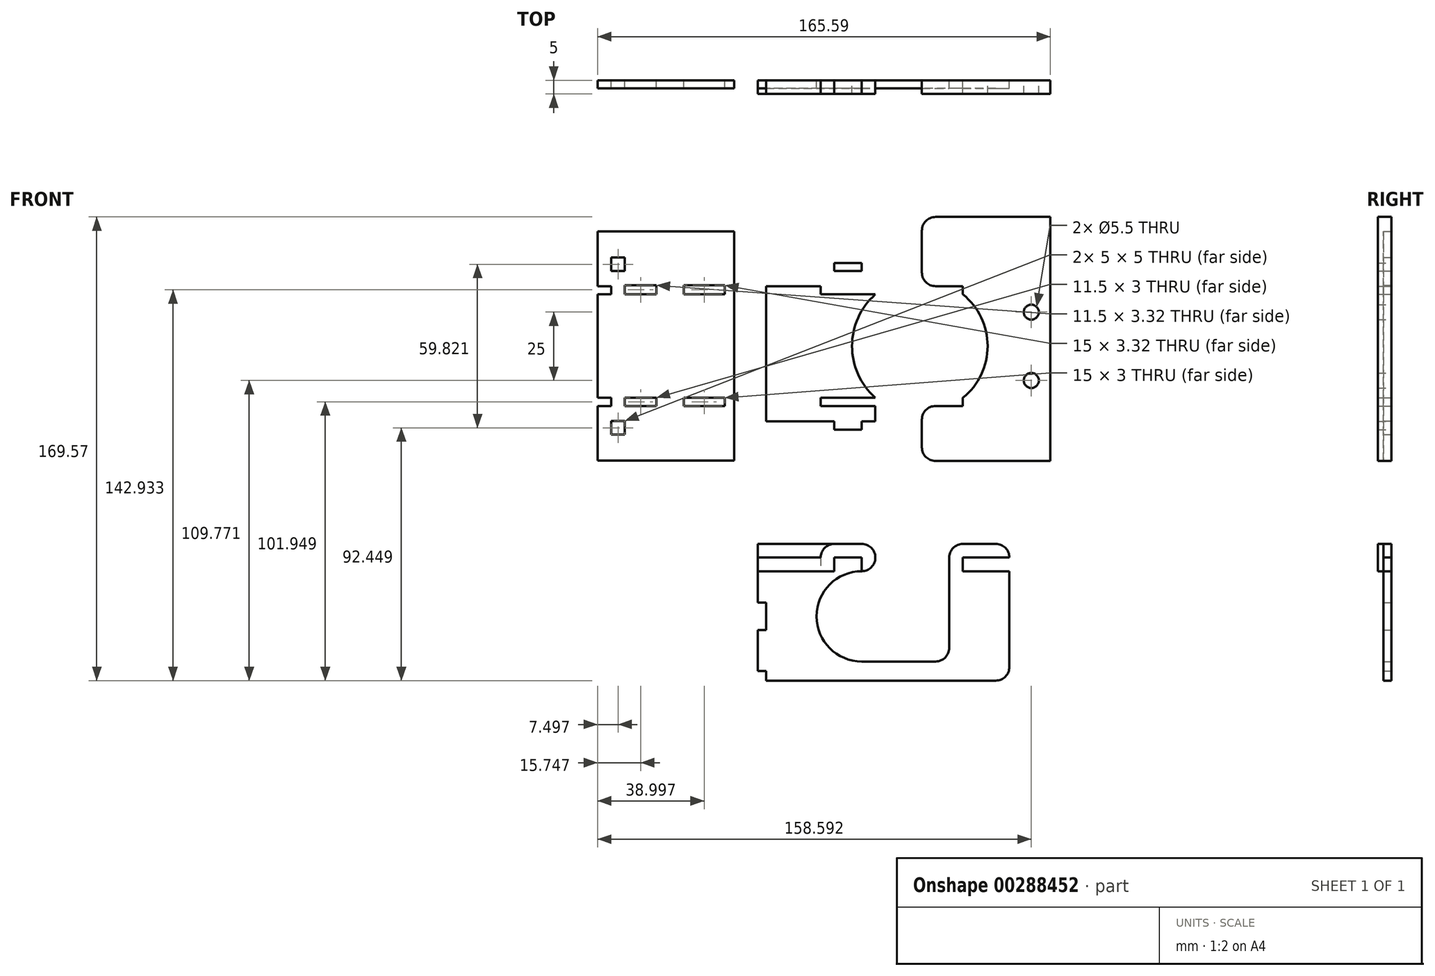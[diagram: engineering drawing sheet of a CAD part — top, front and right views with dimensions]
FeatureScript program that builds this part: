
annotation { "Feature Type Name" : "Feature", "Feature Type Description" : "" }
export const myFeature = defineFeature(function(context is Context, id is Id, definition is map)
    precondition{}
    {
        {
            var Q0;
            Q0=qCreatedBy(makeId("Front.planeOp"),FACE);
            var sketch = newSketch(context, id + "F0", { "sketchPlane" : qUnion([Q0])});
            skLineSegment(sketch, "E0.right", {"start": v(-7.94, 96.43) * mm, "end": v(-7.94, 31.43) * mm});
            skCircle(sketch, "E1", {"center": v(-14.94, 76.43) * mm, "radius": 2.75 * mm});
            skCircle(sketch, "E2", {"center": v(-14.94, 51.43) * mm, "radius": 2.75 * mm});
            skLineSegment(sketch, "E3", {"start": v(-7.94, 63.93) * mm, "end": v(-14.94, 63.93) * mm, "construction": true});
            skLineSegment(sketch, "E4", {"start": v(-14.94, 63.93) * mm, "end": v(-111.94, 63.93) * mm, "construction": true});
            skPoint(sketch, "E5.middle", {"position": v(-52.94, 63.93) * mm});
            skLineSegment(sketch, "E6", {"start": v(-71.94, 82.93) * mm, "end": v(-71.94, 91.43) * mm, "construction": true});
            skLineSegment(sketch, "E7", {"start": v(-71.94, 91.43) * mm, "end": v(-71.94, 82.93) * mm, "construction": true});
            skLineSegment(sketch, "E8", {"start": v(-71.94, 42.1) * mm, "end": v(-71.94, 36.43) * mm, "construction": true});
            skLineSegment(sketch, "E9", {"start": v(-71.94, 85.93) * mm, "end": v(-111.94, 85.93) * mm});
            skLineSegment(sketch, "E10", {"start": v(-111.94, 85.93) * mm, "end": v(-111.94, 91.43) * mm});
            skLineSegment(sketch, "E11", {"start": v(-111.94, 91.43) * mm, "end": v(-71.94, 91.43) * mm});
            skLineSegment(sketch, "E12", {"start": v(-71.94, 42.1) * mm, "end": v(-111.94, 42.1) * mm});
            skLineSegment(sketch, "E13", {"start": v(-111.94, 42.1) * mm, "end": v(-111.94, 36.43) * mm});
            skLineSegment(sketch, "E14", {"start": v(-111.94, 36.43) * mm, "end": v(-71.94, 36.43) * mm});
            skLineSegment(sketch, "E15", {"start": v(-111.94, 91.43) * mm, "end": v(-111.94, 94.43) * mm});
            skLineSegment(sketch, "E16", {"start": v(-111.94, 33.43) * mm, "end": v(-111.94, 42.1) * mm});
            skLineSegment(sketch, "E17", {"start": v(-111.94, 42.1) * mm, "end": v(-111.94, 45.1) * mm});
            skLineSegment(sketch, "E18", {"start": v(-111.94, 85.93) * mm, "end": v(-111.94, 80.93) * mm});
            skLineSegment(sketch, "E19", {"start": v(-71.94, 82.93) * mm, "end": v(-71.94, 85.93) * mm});
            skLineSegment(sketch, "E20", {"start": v(-111.94, 91.43) * mm, "end": v(-91.94, 91.43) * mm});
            skLineSegment(sketch, "E21", {"start": v(-7.94, 63.93) * mm, "end": v(-22.94, 63.93) * mm, "construction": true});
            skLineSegment(sketch, "E22", {"start": v(-22.94, 63.93) * mm, "end": v(-22.94, 96.43) * mm, "construction": true});
            skLineSegment(sketch, "E23", {"start": v(-22.94, 85.93) * mm, "end": v(-22.94, 91.43) * mm});
            skLineSegment(sketch, "E24", {"start": v(-22.94, 42.1) * mm, "end": v(-22.94, 36.43) * mm});
            skLineSegment(sketch, "E25.trimOffspring", {"start": v(-22.94, 63.93) * mm, "end": v(-22.94, 31.43) * mm, "construction": true});
            skPoint(sketch, "E26.end.orphan", {"position": v(-54.94, 91.43) * mm});
            skPoint(sketch, "E27.end.orphan", {"position": v(-54.94, 36.43) * mm});
            skLineSegment(sketch, "E28", {"start": v(-54.94, 91.43) * mm, "end": v(-54.94, 85.93) * mm});
            skLineSegment(sketch, "E29", {"start": v(-54.94, 91.43) * mm, "end": v(-22.94, 91.43) * mm});
            skLineSegment(sketch, "E30", {"start": v(-22.94, 85.93) * mm, "end": v(-54.94, 85.93) * mm});
            skLineSegment(sketch, "E31", {"start": v(-54.94, 42.1) * mm, "end": v(-22.94, 42.1) * mm});
            skLineSegment(sketch, "E32", {"start": v(-22.94, 36.43) * mm, "end": v(-54.94, 36.43) * mm});
            skLineSegment(sketch, "E33.trimOffspring", {"start": v(-54.94, 42.1) * mm, "end": v(-54.94, 36.43) * mm});
            skLineSegment(sketch, "E34", {"start": v(-22.94, 80.93) * mm, "end": v(-22.94, 85.93) * mm});
            skLineSegment(sketch, "E35", {"start": v(-71.94, 85.93) * mm, "end": v(-54.94, 85.93) * mm});
            skLineSegment(sketch, "E36", {"start": v(-71.94, 42.1) * mm, "end": v(-54.94, 42.1) * mm});
            skLineSegment(sketch, "E37.trimOffspring", {"start": v(-71.94, 82.93) * mm, "end": v(-71.94, 85.93) * mm, "construction": true});
            skLineSegment(sketch, "E38", {"start": v(-22.94, 91.43) * mm, "end": v(-22.94, 96.43) * mm});
            skLineSegment(sketch, "E39", {"start": v(-22.94, 36.43) * mm, "end": v(-22.94, 31.43) * mm});
            skLineSegment(sketch, "E40", {"start": v(-71.94, 36.43) * mm, "end": v(-71.94, 33.43) * mm});
            skLineSegment(sketch, "E41", {"start": v(-76.94, 33.43) * mm, "end": v(-111.94, 33.43) * mm});
            skLineSegment(sketch, "E42", {"start": v(-71.94, 91.43) * mm, "end": v(-71.94, 94.43) * mm});
            skLineSegment(sketch, "E43", {"start": v(-76.94, 94.43) * mm, "end": v(-111.94, 94.43) * mm});
            skLineSegment(sketch, "E44", {"start": v(-111.94, 85.93) * mm, "end": v(-111.94, 82.93) * mm});
            skLineSegment(sketch, "E45", {"start": v(-111.94, 82.93) * mm, "end": v(-22.94, 82.93) * mm});
            skLineSegment(sketch, "E46", {"start": v(-22.94, 42.1) * mm, "end": v(-22.94, 45.1) * mm});
            skLineSegment(sketch, "E47", {"start": v(-22.94, 45.1) * mm, "end": v(-111.94, 45.1) * mm});
            skPoint(sketch, "E48.orphan", {"position": v(-22.94, 47.1) * mm});
            skLineSegment(sketch, "E49", {"start": v(-71.94, 91.43) * mm, "end": v(-71.94, 85.93) * mm});
            skLineSegment(sketch, "E50", {"start": v(-71.94, 42.1) * mm, "end": v(-71.94, 36.43) * mm});
            skLineSegment(sketch, "E51.trimOffspring", {"start": v(-111.94, 94.43) * mm, "end": v(-111.94, 80.93) * mm, "construction": true});
            skLineSegment(sketch, "E52.bottom", {"start": v(-111.94, 104.22) * mm, "end": v(-114.94, 104.22) * mm});
            skLineSegment(sketch, "E52.top", {"start": v(-111.94, 18.4) * mm, "end": v(-114.94, 18.4) * mm});
            skLineSegment(sketch, "E52.left", {"start": v(-111.94, 104.22) * mm, "end": v(-111.94, 18.4) * mm});
            skLineSegment(sketch, "E53", {"start": v(-71.94, 42.1) * mm, "end": v(-71.94, 45.1) * mm});
            skLineSegment(sketch, "E54.top", {"start": v(-22.94, 21.99) * mm, "end": v(-54.94, 21.99) * mm});
            skLineSegment(sketch, "E54.left", {"start": v(-22.94, 36.43) * mm, "end": v(-22.94, 29.2) * mm});
            skLineSegment(sketch, "E54.right", {"start": v(-54.94, 36.43) * mm, "end": v(-54.94, 21.99) * mm});
            skLineSegment(sketch, "E55.bottom", {"start": v(-22.94, 91.43) * mm, "end": v(-54.94, 91.43) * mm});
            skLineSegment(sketch, "E55.top", {"start": v(-22.94, 111.23) * mm, "end": v(-54.94, 111.23) * mm});
            skLineSegment(sketch, "E55.right", {"start": v(-54.94, 91.43) * mm, "end": v(-54.94, 111.23) * mm});
            skLineSegment(sketch, "E56", {"start": v(-14.94, 76.43) * mm, "end": v(-44.94, 76.43) * mm, "construction": true});
            skLineSegment(sketch, "E57", {"start": v(-44.94, 85.93) * mm, "end": v(-44.94, 111.23) * mm, "construction": true});
            skLineSegment(sketch, "E58", {"start": v(-44.94, 45.1) * mm, "end": v(-44.94, 42.1) * mm});
            skLineSegment(sketch, "E59", {"start": v(-44.94, 42.1) * mm, "end": v(-44.94, 45.1) * mm});
            skLineSegment(sketch, "E60", {"start": v(-44.94, 82.93) * mm, "end": v(-44.94, 85.93) * mm});
            skPoint(sketch, "E61.trimOffspring.end.orphan", {"position": v(-54.94, 82.93) * mm});
            skPoint(sketch, "E62.start.orphan", {"position": v(-54.94, 45.1) * mm});
            skLineSegment(sketch, "E63.trimOffspring", {"start": v(-44.94, 42.1) * mm, "end": v(-44.94, 21.99) * mm, "construction": true});
            skLineSegment(sketch, "E64", {"start": v(-111.94, 42.1) * mm, "end": v(-111.94, 36.43) * mm, "construction": true});
            skLineSegment(sketch, "E65", {"start": v(-86.94, -8.34) * mm, "end": v(-76.94, -8.34) * mm, "construction": true});
            skPoint(sketch, "E65.endSnap0", {"position": v(-22.94, 29.2) * mm});
            skLineSegment(sketch, "E66", {"start": v(-86.94, -8.34) * mm, "end": v(-76.94, -8.34) * mm});
            skLineSegment(sketch, "E67", {"start": v(-22.94, -53.34) * mm, "end": v(-22.94, -18.34) * mm});
            skLineSegment(sketch, "E68", {"start": v(-44.94, -13.34) * mm, "end": v(-44.94, -46.34) * mm, "construction": true});
            skLineSegment(sketch, "E69", {"start": v(-71.94, 45.1) * mm, "end": v(-71.94, 36.43) * mm, "construction": true});
            skLineSegment(sketch, "E70", {"start": v(-91.94, -18.34) * mm, "end": v(-91.94, -58.34) * mm, "construction": true});
            skLineSegment(sketch, "E71.trimOffspring", {"start": v(-39.94, -8.34) * mm, "end": v(-27.94, -8.34) * mm, "construction": true});
            skLineSegment(sketch, "E72.trimOffspring", {"start": v(-39.94, -8.34) * mm, "end": v(-27.94, -8.34) * mm});
            skLineSegment(sketch, "E73", {"start": v(-22.94, -18.34) * mm, "end": v(-22.94, -53.34) * mm});
            skLineSegment(sketch, "E74", {"start": v(-27.94, -58.34) * mm, "end": v(-111.94, -58.34) * mm});
            skLineSegment(sketch, "E75", {"start": v(-66.94, -51.34) * mm, "end": v(-49.94, -51.34) * mm});
            skLineSegment(sketch, "E76", {"start": v(-44.94, -46.34) * mm, "end": v(-44.94, -13.34) * mm});
            skArc(sketch, "E77.filletArc", {"start": v(-49.94, -51.34) * mm, "mid": v(-46.4, -49.87) * mm, "end": v(-44.94, -46.34) * mm});
            skPoint(sketch, "E78.visualSharp", {"position": v(-71.94, -8.34) * mm});
            skArc(sketch, "E78.filletArc", {"start": v(-71.94, -13.34) * mm, "mid": v(-73.4, -9.8) * mm, "end": v(-76.94, -8.34) * mm});
            skArc(sketch, "E79.filletArc", {"start": v(-39.94, -8.34) * mm, "mid": v(-43.47, -9.8) * mm, "end": v(-44.94, -13.34) * mm});
            skPoint(sketch, "E80.visualSharp", {"position": v(-22.94, -8.34) * mm});
            skArc(sketch, "E80.filletArc", {"start": v(-22.94, -13.34) * mm, "mid": v(-24.4, -9.8) * mm, "end": v(-27.94, -8.34) * mm});
            skArc(sketch, "E81.filletArc", {"start": v(-27.94, -58.34) * mm, "mid": v(-24.4, -56.87) * mm, "end": v(-22.94, -53.34) * mm});
            skLineSegment(sketch, "E82", {"start": v(-111.94, -34.84) * mm, "end": v(-111.94, -29.84) * mm});
            skLineSegment(sketch, "E83", {"start": v(-111.94, -29.84) * mm, "end": v(-111.94, -39.84) * mm});
            skLineSegment(sketch, "E84", {"start": v(-111.94, -39.84) * mm, "end": v(-114.94, -39.84) * mm});
            skLineSegment(sketch, "E85", {"start": v(-114.94, -29.84) * mm, "end": v(-111.94, -29.84) * mm});
            skLineSegment(sketch, "E86", {"start": v(-114.94, 104.22) * mm, "end": v(-114.94, 18.4) * mm});
            skLineSegment(sketch, "E87", {"start": v(-163.53, 82.93) * mm, "end": v(-152.03, 82.93) * mm, "construction": true});
            skLineSegment(sketch, "E88", {"start": v(-111.94, 42.1) * mm, "end": v(-114.94, 42.1) * mm, "construction": true});
            skLineSegment(sketch, "E89", {"start": v(-163.53, 45.1) * mm, "end": v(-152.03, 45.1) * mm, "construction": true});
            skLineSegment(sketch, "E90.trimOffspring", {"start": v(-111.94, -39.84) * mm, "end": v(-111.94, -29.84) * mm});
            skLineSegment(sketch, "E91", {"start": v(-163.53, 86.26) * mm, "end": v(-152.03, 86.26) * mm});
            skLineSegment(sketch, "E92", {"start": v(-127.03, 86.26) * mm, "end": v(-127.03, 82.93) * mm});
            skLineSegment(sketch, "E93", {"start": v(-142.03, 82.93) * mm, "end": v(-142.03, 86.26) * mm});
            skLineSegment(sketch, "E94", {"start": v(-152.03, 86.26) * mm, "end": v(-152.03, 82.93) * mm});
            skLineSegment(sketch, "E95", {"start": v(-142.03, 42.1) * mm, "end": v(-142.03, 45.1) * mm});
            skLineSegment(sketch, "E96.trimOffspring", {"start": v(-152.03, 45.1) * mm, "end": v(-152.03, 42.1) * mm});
            skLineSegment(sketch, "E97.trimOffspring", {"start": v(-127.03, 42.1) * mm, "end": v(-142.03, 42.1) * mm, "construction": true});
            skLineSegment(sketch, "E98.trimOffspring", {"start": v(-152.03, 42.1) * mm, "end": v(-163.53, 42.1) * mm, "construction": true});
            skLineSegment(sketch, "E99.trimOffspring", {"start": v(-142.03, 45.1) * mm, "end": v(-130.53, 45.1) * mm, "construction": true});
            skLineSegment(sketch, "E100.trimOffspring", {"start": v(-152.03, 86.26) * mm, "end": v(-163.53, 86.26) * mm, "construction": true});
            skLineSegment(sketch, "E101.trimOffspring", {"start": v(-142.03, 82.93) * mm, "end": v(-130.53, 82.93) * mm, "construction": true});
            skLineSegment(sketch, "E102.trimOffspring", {"start": v(-142.03, 86.26) * mm, "end": v(-127.03, 86.26) * mm});
            skLineSegment(sketch, "E103.trimOffspring", {"start": v(-114.94, 82.93) * mm, "end": v(-111.94, 82.93) * mm, "construction": true});
            skLineSegment(sketch, "E104.top", {"start": v(-163.53, 82.93) * mm, "end": v(-152.03, 82.93) * mm});
            skLineSegment(sketch, "E105.top", {"start": v(-142.03, 82.93) * mm, "end": v(-130.53, 82.93) * mm});
            skLineSegment(sketch, "E105.left", {"start": v(-142.03, 86.26) * mm, "end": v(-142.03, 82.93) * mm});
            skLineSegment(sketch, "E106.bottom", {"start": v(-164.07, 45.1) * mm, "end": v(-152.03, 45.1) * mm});
            skLineSegment(sketch, "E106.top", {"start": v(-163.53, 42.1) * mm, "end": v(-152.03, 42.1) * mm});
            skLineSegment(sketch, "E107.bottom", {"start": v(-142.03, 45.1) * mm, "end": v(-127.03, 45.1) * mm});
            skLineSegment(sketch, "E107.top", {"start": v(-142.03, 42.1) * mm, "end": v(-127.03, 42.1) * mm});
            skLineSegment(sketch, "E107.left", {"start": v(-142.03, 45.1) * mm, "end": v(-142.03, 42.1) * mm});
            skLineSegment(sketch, "E108.trimOffspring", {"start": v(-71.94, -13.34) * mm, "end": v(-71.94, -13.34) * mm});
            skPoint(sketch, "E109.orphan", {"position": v(-22.94, -58.34) * mm});
            skLineSegment(sketch, "E110", {"start": v(-123.53, 105.93) * mm, "end": v(-172.03, 105.93) * mm});
            skLineSegment(sketch, "E111", {"start": v(-123.53, 22.1) * mm, "end": v(-172.03, 22.1) * mm});
            skLineSegment(sketch, "E112", {"start": v(-22.94, -13.34) * mm, "end": v(-39.94, -13.34) * mm});
            skLineSegment(sketch, "E113", {"start": v(-39.94, -13.34) * mm, "end": v(-39.94, -18.34) * mm});
            skLineSegment(sketch, "E114", {"start": v(-39.94, -18.34) * mm, "end": v(-22.94, -18.34) * mm});
            skLineSegment(sketch, "E115.trimOffspring", {"start": v(-39.94, 36.43) * mm, "end": v(-39.94, 45.1) * mm});
            skLineSegment(sketch, "E116.trimOffspring", {"start": v(-39.94, 82.93) * mm, "end": v(-39.94, 91.43) * mm});
            skLineSegment(sketch, "E117", {"start": v(-91.94, -13.34) * mm, "end": v(-91.94, -13.34) * mm});
            skLineSegment(sketch, "E118", {"start": v(-114.94, -29.84) * mm, "end": v(-114.94, -18.34) * mm});
            skLineSegment(sketch, "E119", {"start": v(-114.94, -39.84) * mm, "end": v(-114.94, -54.84) * mm});
            skLineSegment(sketch, "E120", {"start": v(-114.94, -54.84) * mm, "end": v(-111.94, -54.84) * mm});
            skLineSegment(sketch, "E121", {"start": v(-111.94, -54.84) * mm, "end": v(-111.94, -58.34) * mm});
            skArc(sketch, "E122", {"start": v(-39.94, 45.1) * mm, "mid": v(-30.9, 64.02) * mm, "end": v(-39.94, 82.93) * mm});
            skLineSegment(sketch, "E123", {"start": v(-91.94, -18.34) * mm, "end": v(-111.94, -18.34) * mm});
            skLineSegment(sketch, "E124", {"start": v(-111.94, -18.34) * mm, "end": v(-114.94, -18.34) * mm});
            skLineSegment(sketch, "E125", {"start": v(-142.03, 45.1) * mm, "end": v(-130.53, 45.1) * mm});
            skLineSegment(sketch, "E126", {"start": v(-127.03, 42.1) * mm, "end": v(-127.03, 45.1) * mm});
            skLineSegment(sketch, "E127", {"start": v(-130.53, 82.93) * mm, "end": v(-127.03, 82.93) * mm});
            skLineSegment(sketch, "E128", {"start": v(-152.03, 45.1) * mm, "end": v(-163.53, 45.1) * mm});
            skLineSegment(sketch, "E129", {"start": v(-163.53, 42.1) * mm, "end": v(-163.53, 45.1) * mm});
            skLineSegment(sketch, "E130", {"start": v(-91.94, -18.34) * mm, "end": v(-86.94, -18.34) * mm});
            skLineSegment(sketch, "E131", {"start": v(-86.94, -18.34) * mm, "end": v(-86.94, -13.34) * mm});
            skLineSegment(sketch, "E132", {"start": v(-91.94, -13.34) * mm, "end": v(-86.94, -13.34) * mm});
            skLineSegment(sketch, "E133", {"start": v(-86.94, -13.34) * mm, "end": v(-86.94, 110) * mm, "construction": true});
            skArc(sketch, "E134", {"start": v(-71.94, 82.93) * mm, "mid": v(-80.46, 64.02) * mm, "end": v(-71.94, 45.1) * mm});
            skLineSegment(sketch, "E135", {"start": v(-86.94, 42.1) * mm, "end": v(-86.94, 45.1) * mm});
            skLineSegment(sketch, "E136", {"start": v(-86.94, 82.93) * mm, "end": v(-86.94, 85.93) * mm});
            skPoint(sketch, "E137.end.orphan", {"position": v(-91.94, 42.1) * mm});
            skPoint(sketch, "E137.start.orphan", {"position": v(-91.94, 45.1) * mm});
            skLineSegment(sketch, "E138", {"start": v(-86.94, 33.43) * mm, "end": v(-86.94, 36.43) * mm});
            skLineSegment(sketch, "E139", {"start": v(-86.94, 91.43) * mm, "end": v(-86.94, 94.43) * mm});
            skLineSegment(sketch, "E140", {"start": v(-91.94, -13.34) * mm, "end": v(-114.94, -13.34) * mm});
            skLineSegment(sketch, "E141", {"start": v(-114.94, -13.34) * mm, "end": v(-114.94, -8.34) * mm});
            skLineSegment(sketch, "E142", {"start": v(-86.94, -8.34) * mm, "end": v(-86.94, -8.34) * mm});
            skLineSegment(sketch, "E143", {"start": v(-163.53, 45.1) * mm, "end": v(-164.07, 45.1) * mm});
            skLineSegment(sketch, "E144", {"start": v(-172.03, 45.1) * mm, "end": v(-168.53, 45.1) * mm});
            skLineSegment(sketch, "E145", {"start": v(-168.53, 45.1) * mm, "end": v(-168.53, 42.1) * mm});
            skLineSegment(sketch, "E146", {"start": v(-168.53, 42.1) * mm, "end": v(-172.03, 42.1) * mm});
            skPoint(sketch, "E147.orphan", {"position": v(-167.03, 42.1) * mm});
            skPoint(sketch, "E148.orphan", {"position": v(-173.53, 45.1) * mm});
            skLineSegment(sketch, "E149.trimOffspring", {"start": v(-168.53, 45.1) * mm, "end": v(-172.03, 45.1) * mm});
            skLineSegment(sketch, "E150", {"start": v(-168.53, 85.93) * mm, "end": v(-168.53, 82.93) * mm});
            skLineSegment(sketch, "E151", {"start": v(-168.53, 82.93) * mm, "end": v(-172.03, 82.93) * mm});
            skLineSegment(sketch, "E152", {"start": v(-168.53, 85.93) * mm, "end": v(-172.03, 85.93) * mm});
            skLineSegment(sketch, "E153.trimOffspring", {"start": v(-163.53, 82.93) * mm, "end": v(-163.53, 86.26) * mm});
            skLineSegment(sketch, "E154", {"start": v(-86.94, 33.43) * mm, "end": v(-78.42, 33.43) * mm});
            skLineSegment(sketch, "E155", {"start": v(-78.42, 33.43) * mm, "end": v(-76.94, 33.43) * mm});
            skLineSegment(sketch, "E156", {"start": v(-91.94, -13.34) * mm, "end": v(-91.94, -18.34) * mm});
            skLineSegment(sketch, "E157", {"start": v(-86.94, -13.34) * mm, "end": v(-71.94, -13.34) * mm});
            skLineSegment(sketch, "E158", {"start": v(-86.94, -18.34) * mm, "end": v(-76.94, -18.34) * mm});
            skArc(sketch, "E159.filletArc", {"start": v(-86.94, -8.34) * mm, "mid": v(-90.47, -9.8) * mm, "end": v(-91.94, -13.34) * mm});
            skLineSegment(sketch, "E160", {"start": v(-86.94, -8.34) * mm, "end": v(-114.94, -8.34) * mm});
            skLineSegment(sketch, "E161", {"start": v(-114.94, -18.34) * mm, "end": v(-114.94, -13.34) * mm});
            skLineSegment(sketch, "E162", {"start": v(-76.94, -13.34) * mm, "end": v(-76.94, -18.34) * mm});
            skLineSegment(sketch, "E163", {"start": v(-76.94, 33.43) * mm, "end": v(-76.94, 36.43) * mm});
            skLineSegment(sketch, "E164", {"start": v(-76.94, 94.43) * mm, "end": v(-76.94, 91.43) * mm});
            skLineSegment(sketch, "E165.trimOffspring", {"start": v(-71.94, 33.43) * mm, "end": v(-71.94, -8.34) * mm, "construction": true});
            skPoint(sketch, "E166.newPointA", {"position": v(-71.94, -18.34) * mm});
            skArc(sketch, "E166.filletArc", {"start": v(-76.94, -18.34) * mm, "mid": v(-73.4, -16.87) * mm, "end": v(-71.94, -13.34) * mm});
            skLineSegment(sketch, "E167", {"start": v(-168.53, 36.6) * mm, "end": v(-163.53, 36.6) * mm});
            skLineSegment(sketch, "E168", {"start": v(-163.53, 36.6) * mm, "end": v(-163.53, 31.6) * mm});
            skLineSegment(sketch, "E169", {"start": v(-163.53, 31.6) * mm, "end": v(-168.53, 31.6) * mm});
            skLineSegment(sketch, "E170", {"start": v(-168.53, 31.6) * mm, "end": v(-168.53, 36.6) * mm});
            skLineSegment(sketch, "E171", {"start": v(-168.53, 91.43) * mm, "end": v(-168.53, 96.43) * mm});
            skLineSegment(sketch, "E172", {"start": v(-168.53, 96.43) * mm, "end": v(-163.53, 96.43) * mm});
            skLineSegment(sketch, "E173", {"start": v(-163.53, 96.43) * mm, "end": v(-163.53, 91.43) * mm});
            skLineSegment(sketch, "E174", {"start": v(-163.53, 91.43) * mm, "end": v(-168.53, 91.43) * mm});
            skLineSegment(sketch, "E175", {"start": v(-123.53, 22.1) * mm, "end": v(-125.95, 22.1) * mm});
            skLineSegment(sketch, "E176", {"start": v(-123.53, 42.1) * mm, "end": v(-123.53, 22.1) * mm});
            skLineSegment(sketch, "E177", {"start": v(-123.53, 22.1) * mm, "end": v(-123.53, 105.93) * mm});
            skLineSegment(sketch, "E178", {"start": v(-200.22, 72.26) * mm, "end": v(-197.35, 102.21) * mm});
            skLineSegment(sketch, "E179", {"start": v(-123.53, 22.1) * mm, "end": v(-191.87, 22.1) * mm, "construction": true});
            skPoint(sketch, "E179.endSnap0", {"position": v(-124.74, 22.1) * mm});
            skLineSegment(sketch, "E180", {"start": v(-123.53, 22.1) * mm, "end": v(-173.53, 22.1) * mm});
            skLineSegment(sketch, "E181", {"start": v(-173.53, 22.1) * mm, "end": v(-173.53, 42.1) * mm});
            skLineSegment(sketch, "E182", {"start": v(-173.53, 105.93) * mm, "end": v(-172.03, 105.93) * mm});
            skLineSegment(sketch, "E183", {"start": v(-168.53, 85.93) * mm, "end": v(-173.53, 85.93) * mm});
            skLineSegment(sketch, "E184", {"start": v(-173.53, 82.93) * mm, "end": v(-172.03, 82.93) * mm});
            skLineSegment(sketch, "E185", {"start": v(-172.03, 45.1) * mm, "end": v(-173.53, 45.1) * mm});
            skLineSegment(sketch, "E186", {"start": v(-172.03, 42.1) * mm, "end": v(-173.53, 42.1) * mm});
            skLineSegment(sketch, "E187.trimOffspring", {"start": v(-173.53, 45.1) * mm, "end": v(-173.53, 82.93) * mm});
            skLineSegment(sketch, "E188.trimOffspring", {"start": v(-173.53, 85.93) * mm, "end": v(-173.53, 105.93) * mm});
            skLineSegment(sketch, "E189", {"start": v(-66.94, -51.34) * mm, "end": v(-76.94, -51.34) * mm});
            skArc(sketch, "E190", {"start": v(-76.94, -18.34) * mm, "mid": v(-93.44, -34.84) * mm, "end": v(-76.94, -51.34) * mm});
            skLineSegment(sketch, "E191", {"start": v(-91.94, -13.34) * mm, "end": v(-91.94, 36.43) * mm, "construction": true});
            skLineSegment(sketch, "E192", {"start": v(-91.94, 85.93) * mm, "end": v(-91.94, 82.93) * mm});
            skLineSegment(sketch, "E193", {"start": v(-91.94, 42.1) * mm, "end": v(-91.94, 45.1) * mm});
            skLineSegment(sketch, "E194.trimOffspring", {"start": v(-91.94, 82.93) * mm, "end": v(-91.94, 85.93) * mm, "construction": true});
            skLineSegment(sketch, "E195.trimOffspring", {"start": v(-91.94, 42.1) * mm, "end": v(-91.94, 45.1) * mm, "construction": true});
            skLineSegment(sketch, "E196.trimOffspring", {"start": v(-91.94, 91.43) * mm, "end": v(-91.94, 110.09) * mm, "construction": true});
            skLineSegment(sketch, "E197", {"start": v(-7.94, 96.43) * mm, "end": v(-7.94, 111.23) * mm});
            skLineSegment(sketch, "E198", {"start": v(-7.94, 111.23) * mm, "end": v(-22.94, 111.23) * mm});
            skLineSegment(sketch, "E199", {"start": v(-22.94, 21.99) * mm, "end": v(-7.94, 21.99) * mm});
            skLineSegment(sketch, "E200", {"start": v(-7.94, 21.99) * mm, "end": v(-7.94, 31.43) * mm});
            skSolve(sketch);
        }
        {
            var Q0;
            Q0=makeQuery(id+"F0.imprint","IMPRINT",FACE,{"disambiguationData":[TD([[makeQuery(id+"F0.imprint","IMPRINT",EDGE,{"derivedFrom":sQuery(id+"F0.wireOp",EDGE,"E66")}),-1.0]])]});
            var Q1;
            Q1=makeQuery(id+"F0.imprint","IMPRINT",FACE,{"disambiguationData":[TD([[makeQuery(id+"F0.imprint","IMPRINT",EDGE,{"derivedFrom":sQuery(id+"F0.wireOp",EDGE,"E140")}),-1.0]])]});
            var Q2;
            Q2=makeQuery(id+"F0.imprint","IMPRINT",FACE,{"disambiguationData":[TD([[makeQuery(id+"F0.imprint","IMPRINT",EDGE,{"derivedFrom":sQuery(id+"F0.wireOp",EDGE,"E131")}),-1.0]])]});
            var Q3;
            Q3=makeQuery(id+"F0.imprint","IMPRINT",FACE,{"disambiguationData":[TD([[makeQuery(id+"F0.imprint","IMPRINT",EDGE,{"derivedFrom":sQuery(id+"F0.wireOp",EDGE,"E72.trimOffspring")}),-1.0]])]});
            var Q4;
            {var subQ2=sQuery(id+"F0.wireOp",EDGE,"E162");Q4=makeQuery(id+"F0.imprint","IMPRINT",FACE,{"disambiguationData":[TD([[makeQuery(id+"F0.imprint","IMPRINT",EDGE,{"derivedFrom":subQ2}),1.0]])]});}
            var Q5;
            {var subQ0=sQuery(id+"F0.wireOp",EDGE,"E166.filletArc");Q5=makeQuery(id+"F0.imprint","IMPRINT",FACE,{"disambiguationData":[TD([[makeQuery(id+"F0.imprint","IMPRINT",EDGE,{"derivedFrom":subQ0}),-1.0]])]});}
            var Q6;
            Q6=makeQuery(id+"F0.imprint","IMPRINT",FACE,{"disambiguationData":[TD([[makeQuery(id+"F0.imprint","IMPRINT",EDGE,{"derivedFrom":sQuery(id+"F0.wireOp",EDGE,"E130")}),1.0]])]});
            extrude(context, id + "F1", {"entities" : qUnion([Q0, Q1, Q2, Q3, Q4, Q5, Q6]), "depth" : 3 * mm});
        }
        {
            var Q0;
            Q0=makeQuery(id+"F0.imprint","IMPRINT",FACE,{"disambiguationData":[TD([[makeQuery(id+"F0.imprint","IMPRINT",EDGE,{"derivedFrom":sQuery(id+"F0.wireOp",EDGE,"E91")}),1.0]])]});
            extrude(context, id + "F2", {"entities" : qUnion([Q0]), "depth" : 3 * mm});
        }
        {
            var Q0;
            Q0=makeQuery(id+"F0.imprint","IMPRINT",FACE,{"disambiguationData":[TD([[makeQuery(id+"F0.imprint","IMPRINT",EDGE,{"derivedFrom":sQuery(id+"F0.wireOp",EDGE,"E0.right")}),-1.0]])]});
            var Q1;
            {var subQ1=sQuery(id+"F0.wireOp",EDGE,"E30");var subQ3=sQuery(id+"F0.wireOp",EDGE,"E116.trimOffspring");var subQ4=makeQuery(id+"F0.imprint","INTERSECT",VERTEX,{"derivedFrom":[subQ1,subQ3]});Q1=makeQuery(id+"F0.imprint","IMPRINT",FACE,{"disambiguationData":[TD([[makeQuery(id+"F0.imprint","IMPRINT",EDGE,{"disambiguationData":[TD([[subQ4,1.0]])],"derivedFrom":subQ1}),1.0]])]});}
            var Q2;
            {var subQ0=sQuery(id+"F0.wireOp",EDGE,"E23");Q2=makeQuery(id+"F0.imprint","IMPRINT",FACE,{"disambiguationData":[TD([[makeQuery(id+"F0.imprint","IMPRINT",EDGE,{"derivedFrom":subQ0}),1.0]])]});}
            var Q3;
            {var subQ1=sQuery(id+"F0.wireOp",EDGE,"E28");Q3=makeQuery(id+"F0.imprint","IMPRINT",FACE,{"disambiguationData":[TD([[makeQuery(id+"F0.imprint","IMPRINT",EDGE,{"derivedFrom":subQ1}),1.0]])]});}
            var Q4;
            {var subQ4=sQuery(id+"F0.wireOp",EDGE,"E55.top");Q4=makeQuery(id+"F0.imprint","IMPRINT",FACE,{"disambiguationData":[TD([[makeQuery(id+"F0.imprint","IMPRINT",EDGE,{"derivedFrom":subQ4}),1.0]])]});}
            var Q5;
            {var subQ0=sQuery(id+"F0.wireOp",EDGE,"E46");Q5=makeQuery(id+"F0.imprint","IMPRINT",FACE,{"disambiguationData":[TD([[makeQuery(id+"F0.imprint","IMPRINT",EDGE,{"derivedFrom":subQ0}),1.0]])]});}
            var Q6;
            {var subQ0=sQuery(id+"F0.wireOp",EDGE,"E24");Q6=makeQuery(id+"F0.imprint","IMPRINT",FACE,{"disambiguationData":[TD([[makeQuery(id+"F0.imprint","IMPRINT",EDGE,{"derivedFrom":subQ0}),-1.0]])]});}
            var Q7;
            {var subQ0=sQuery(id+"F0.wireOp",EDGE,"E33.trimOffspring");Q7=makeQuery(id+"F0.imprint","IMPRINT",FACE,{"disambiguationData":[TD([[makeQuery(id+"F0.imprint","IMPRINT",EDGE,{"derivedFrom":subQ0}),1.0]])]});}
            var Q8;
            {var subQ4=sQuery(id+"F0.wireOp",EDGE,"E54.top");Q8=makeQuery(id+"F0.imprint","IMPRINT",FACE,{"disambiguationData":[TD([[makeQuery(id+"F0.imprint","IMPRINT",EDGE,{"derivedFrom":subQ4}),-1.0]])]});}
            extrude(context, id + "F3", {"entities" : qUnion([Q0, Q1, Q2, Q3, Q4, Q5, Q6, Q7, Q8]), "depth" : 5 * mm});
        }
        {
            var Q0;
            {var subQ0=sQuery(id+"F0.wireOp",EDGE,"E134");Q0=makeQuery(id+"F0.imprint","IMPRINT",FACE,{"disambiguationData":[TD([[makeQuery(id+"F0.imprint","IMPRINT",EDGE,{"derivedFrom":subQ0}),-1.0]])]});}
            var Q1;
            {var subQ0=sQuery(id+"F0.wireOp",EDGE,"E50");Q1=makeQuery(id+"F0.imprint","IMPRINT",FACE,{"disambiguationData":[TD([[makeQuery(id+"F0.imprint","IMPRINT",EDGE,{"derivedFrom":subQ0}),-1.0]])]});}
            var Q2;
            {var subQ3=sQuery(id+"F0.wireOp",EDGE,"E135");Q2=makeQuery(id+"F0.imprint","IMPRINT",FACE,{"disambiguationData":[TD([[makeQuery(id+"F0.imprint","IMPRINT",EDGE,{"derivedFrom":subQ3}),1.0]])]});}
            var Q3;
            {var subQ3=sQuery(id+"F0.wireOp",EDGE,"E136");Q3=makeQuery(id+"F0.imprint","IMPRINT",FACE,{"disambiguationData":[TD([[makeQuery(id+"F0.imprint","IMPRINT",EDGE,{"derivedFrom":subQ3}),1.0]])]});}
            var Q4;
            {var subQ6=sQuery(id+"F0.wireOp",EDGE,"E20");Q4=makeQuery(id+"F0.imprint","IMPRINT",FACE,{"disambiguationData":[TD([[makeQuery(id+"F0.imprint","IMPRINT",EDGE,{"derivedFrom":subQ6}),-1.0]])]});}
            var Q5;
            {var subQ0=sQuery(id+"F0.wireOp",EDGE,"E40");Q5=makeQuery(id+"F0.imprint","IMPRINT",FACE,{"disambiguationData":[TD([[makeQuery(id+"F0.imprint","IMPRINT",EDGE,{"derivedFrom":subQ0}),-1.0]])]});}
            var Q6;
            {var subQ0=sQuery(id+"F0.wireOp",EDGE,"E42");Q6=makeQuery(id+"F0.imprint","IMPRINT",FACE,{"disambiguationData":[TD([[makeQuery(id+"F0.imprint","IMPRINT",EDGE,{"derivedFrom":subQ0}),1.0]])]});}
            extrude(context, id + "F4", {"entities" : qUnion([Q0, Q1, Q2, Q3, Q4, Q5, Q6]), "depth" : 5 * mm});
        }
        {
            var Q0;
            Q0=makeQuery(id+"F0.imprint","IMPRINT",FACE,{"disambiguationData":[TD([[makeQuery(id+"F0.imprint","IMPRINT",EDGE,{"derivedFrom":sQuery(id+"F0.wireOp",EDGE,"E123")}),-1.0]])]});
            var Q1;
            Q1=makeQuery(id+"F0.imprint","IMPRINT",FACE,{"disambiguationData":[TD([[makeQuery(id+"F0.imprint","IMPRINT",EDGE,{"derivedFrom":sQuery(id+"F0.wireOp",EDGE,"E130")}),1.0]])]});
            var Q2;
            Q2=makeQuery(id+"F0.imprint","IMPRINT",FACE,{"disambiguationData":[TD([[makeQuery(id+"F0.imprint","IMPRINT",EDGE,{"derivedFrom":sQuery(id+"F0.wireOp",EDGE,"E66")}),-1.0]])]});
            var Q3;
            {var subQ2=sQuery(id+"F0.wireOp",EDGE,"E162");Q3=makeQuery(id+"F0.imprint","IMPRINT",FACE,{"disambiguationData":[TD([[makeQuery(id+"F0.imprint","IMPRINT",EDGE,{"derivedFrom":subQ2}),1.0]])]});}
            extrude(context, id + "F5", {"entities" : qUnion([Q0, Q1, Q2, Q3]), "depth" : 5 * mm});
        }
        {
            var Q0;
            {var subQ0=sQuery(id+"F0.wireOp",EDGE,"E138");Q0=makeQuery(id+"F0.imprint","IMPRINT",FACE,{"disambiguationData":[TD([[makeQuery(id+"F0.imprint","IMPRINT",EDGE,{"derivedFrom":subQ0}),-1.0]])]});}
            var Q1;
            {var subQ0=sQuery(id+"F0.wireOp",EDGE,"E139");Q1=makeQuery(id+"F0.imprint","IMPRINT",FACE,{"disambiguationData":[TD([[makeQuery(id+"F0.imprint","IMPRINT",EDGE,{"derivedFrom":subQ0}),-1.0]])]});}
            var Q2;
            {var subQ3=sQuery(id+"F0.wireOp",EDGE,"E192");Q2=makeQuery(id+"F0.imprint","IMPRINT",FACE,{"disambiguationData":[TD([[makeQuery(id+"F0.imprint","IMPRINT",EDGE,{"derivedFrom":subQ3}),-1.0]])]});}
            var Q3;
            {var subQ3=sQuery(id+"F0.wireOp",EDGE,"E193");Q3=makeQuery(id+"F0.imprint","IMPRINT",FACE,{"disambiguationData":[TD([[makeQuery(id+"F0.imprint","IMPRINT",EDGE,{"derivedFrom":subQ3}),1.0]])]});}
            var Q4;
            {var subQ0=sQuery(id+"F0.wireOp",EDGE,"E136");Q4=makeQuery(id+"F0.imprint","IMPRINT",FACE,{"disambiguationData":[TD([[makeQuery(id+"F0.imprint","IMPRINT",EDGE,{"derivedFrom":subQ0}),1.0]])]});}
            var Q5;
            {var subQ0=sQuery(id+"F0.wireOp",EDGE,"E135");Q5=makeQuery(id+"F0.imprint","IMPRINT",FACE,{"disambiguationData":[TD([[makeQuery(id+"F0.imprint","IMPRINT",EDGE,{"derivedFrom":subQ0}),1.0]])]});}
            extrude(context, id + "F6", {"entities" : qUnion([Q0, Q1, Q2, Q3, Q4, Q5]), "operationType" : NewBodyOperationType.ADD, "depth" : 5 * mm});
        }
        {
            var Q0;
            {var subQ0=sQuery(id+"F0.wireOp",EDGE,"E136");Q0=makeQuery(id+"F0.imprint","IMPRINT",FACE,{"disambiguationData":[TD([[makeQuery(id+"F0.imprint","IMPRINT",EDGE,{"derivedFrom":subQ0}),1.0]])]});}
            var Q1;
            {var subQ0=sQuery(id+"F0.wireOp",EDGE,"E135");Q1=makeQuery(id+"F0.imprint","IMPRINT",FACE,{"disambiguationData":[TD([[makeQuery(id+"F0.imprint","IMPRINT",EDGE,{"derivedFrom":subQ0}),1.0]])]});}
            extrude(context, id + "F7", {"entities" : qUnion([Q0, Q1]), "operationType" : NewBodyOperationType.REMOVE, "depth" : 5 * mm});
        }
        {
            var Q0;
            Q0=makeQuery(id+"F3.opExtrude","SWEPT_EDGE",EDGE,{"disambiguationData":[OSD([sQuery(id+"F0.wireOp",EDGE,"E31"),sQuery(id+"F0.wireOp",EDGE,"E33.trimOffspring"),sQuery(id+"F0.wireOp",EDGE,"E36")])]});
            var Q1;
            Q1=makeQuery(id+"F3.opExtrude","SWEPT_EDGE",EDGE,{"disambiguationData":[OSD([sQuery(id+"F0.wireOp",EDGE,"E28"),sQuery(id+"F0.wireOp",EDGE,"E30"),sQuery(id+"F0.wireOp",EDGE,"E35")])]});
            var Q2;
            Q2=makeQuery(id+"F3.opExtrude","SWEPT_EDGE",EDGE,{"disambiguationData":[OSD([sQuery(id+"F0.wireOp",EDGE,"E54.top"),sQuery(id+"F0.wireOp",EDGE,"E54.right")])]});
            var Q3;
            Q3=makeQuery(id+"F3.opExtrude","SWEPT_EDGE",EDGE,{"disambiguationData":[OSD([sQuery(id+"F0.wireOp",EDGE,"E55.top"),sQuery(id+"F0.wireOp",EDGE,"E55.right")])]});
            fillet(context, id + "F8", {"entities" : qUnion([Q0, Q1, Q2, Q3]), "radius" : 5 * mm, "tangentPropagation" : true, "allowEdgeOverflow" : false});
        }
    });
